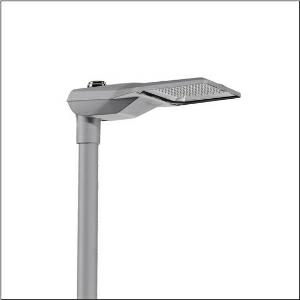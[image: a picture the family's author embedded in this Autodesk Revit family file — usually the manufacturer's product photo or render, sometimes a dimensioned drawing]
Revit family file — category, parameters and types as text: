
# Revit family: streetlight_sl_21_midi___st1_0a_5xe7d47n08mb_32fc
name_source: partatom
category: Lighting Fixtures
units: mm (PartAtom-declared; Revit-internal decimal feet)

## family parameters
Cut with Voids When Loaded = No
Host = Face
Light Source = No
Part Type = Normal
Room Calculation Point = No
Round Connector Dimension = Use Diameter
Shared = No

## types (1)
- --- (1 x LED, 20180 lm, 147 W, 4000K)
    Apparent Load = 147 VA
    CIE Flux Codes = 37 72 97 100 100
    Color Rendering = 70
    Color Temperature = 4000K
    Default Elevation = 1800 mm
    Description = Streetlight SL 21 midi, mast luminaire, primary light control with lens, of PMMA, primary optical cover: cover, of toughened safety glass, transparent, light distribution: ST1.0a, light emission: direct distribution, primary light characteristic: asymmetric, installation type: side-entry, LED, 3G 2.5mm², High Power LED, rated luminous flux: 20.180lm, luminous efficacy: 137lm/W, light colour: 740, colour temperature: 4000K, control gear: NEMA (7pin), control: overheat protection, pre-setting: linear dimming characteristic, constant luminous flux control, time-dependent luminous flux control, flexible luminous flux parameterisation, mains connection: 220..240V, AC, 50/60Hz, connection cable pre-assembled, cable length: 12,5m, wiring characteristics: H05VV-F, start of lifetime: 147W, end of service life: 155W, reduction: 65W, luminaire housing, of diecast aluminium (EN AC-44300), powder-coated, SITECO metallic grey (DB 702S), corrosivity category C5 high according to DIN EN ISO 12944, multi-level sealing system, sealing non-destructively replaceable, inclination adjustable: 0°, 5°, 10°, 15°, length: 644mm, width: 335mm, height: 110mm, spigot size: 42mm (side-entry), mounting height: 4..8m, protection rating (complete): IP66, insulation class (complete): insulation class I (protective earthing), certification: CE, ENEC, ENEC+, VDE, impact resistance: IK10, permissible operating ambient temperature for outdoor applications: -40..+50°C, standard-compliant lighting for roads and squares, packaging unit: 1 piece

Light Distribution: ST1.0a
    Height = 111 mm
    Lamp = 1 x LED
    Lamp Light Flux = 20180 lm
    Lamp Power = 147 W
    Lamp count = 1
    Length = 644 mm
    Luminous efficacy = 137 lm/W
    Manufacturer = Siteco
    ModVariant = No
    Model = 5XE7D47N08MB
    Number of Poles = 1
    OnlyDefault = Yes
    Power Factor = 1
    Product Name = Streetlight SL 21 midi | ST1.0a
    Product group = mast luminaire | pylon top
    ProductGroupID = 6100
    Protection Class = Protection class I
    Protection Degree = IP 66
    RLX_Detail_Level = 1
    RLX_Emergency_Light_Flux = 0 lm
    RLX_Emergency_Type = 0
    RLX_Emergency_Type_DB = No
    RlxData = <blob elided: 26525 chars, md5=d3946678>
    Socket = socket
    Standby Power = 0 W
    System Light Flux = 20180 lm
    System Power = 147 W
    Type Comments = factory setting: luminous flux: 100 % | dim-lin: 254 | 750 mA
    Type Image = l_1294377.jpg
    URL = http://relux.com
    VarID = @adj_135465
    Voltage = 0 V
    Weight = 0.00 kg
    Width = 336 mm

## geometry (parser evidence)
native form markers: Blend x4, Sweep x11
no freeform markers — native parametric forms only
